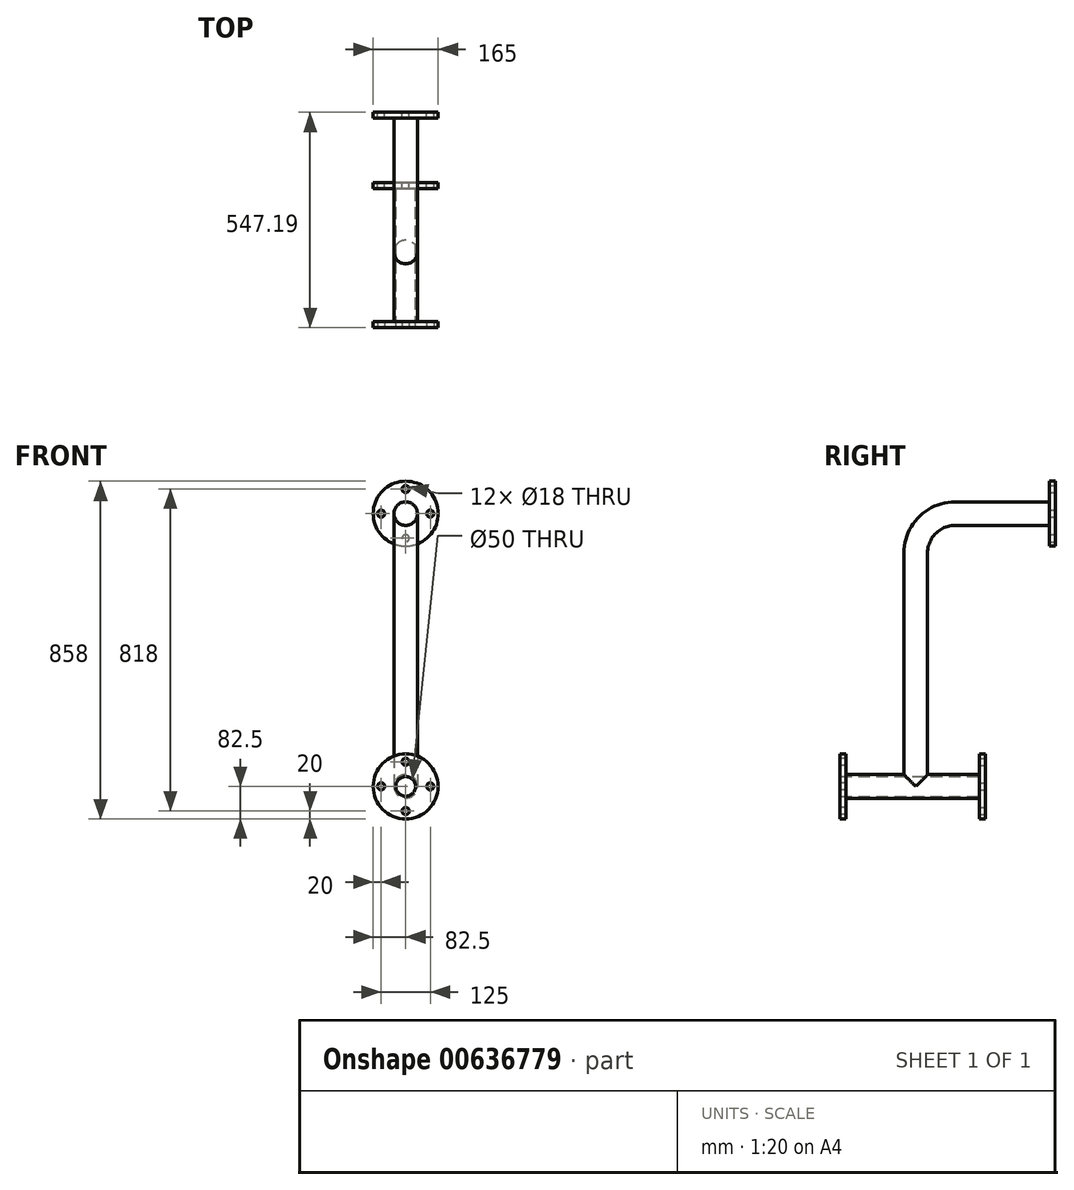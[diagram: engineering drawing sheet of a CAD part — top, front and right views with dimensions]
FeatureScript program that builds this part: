
annotation { "Feature Type Name" : "Feature", "Feature Type Description" : "" }
export const myFeature = defineFeature(function(context is Context, id is Id, definition is map)
    precondition{}
    {
        {
            var Q0;
            Q0=qCreatedBy(makeId("Front.planeOp"),FACE);
            var sketch = newSketch(context, id + "F0", { "sketchPlane" : qUnion([Q0])});
            skCircle(sketch, "E0", {"center": v(0, 0) * mm, "radius": 82.5 * mm});
            skCircle(sketch, "E1", {"center": v(0, 0) * mm, "radius": 30 * mm});
            skSolve(sketch);
        }
        {
            var Q0;
            Q0=qCreatedBy(makeId("Right.planeOp"),FACE);
            var sketch = newSketch(context, id + "F1", { "sketchPlane" : qUnion([Q0])});
            skLineSegment(sketch, "E2", {"start": v(0, 0) * mm, "end": v(-255, 0) * mm});
            skLineSegment(sketch, "E3", {"start": v(-355, -100) * mm, "end": v(-355, -693) * mm});
            skLineSegment(sketch, "E4", {"start": v(-355, -693) * mm, "end": v(-178.56, -693) * mm});
            skLineSegment(sketch, "E5", {"start": v(-355, -693) * mm, "end": v(-547.2, -693) * mm});
            skPoint(sketch, "E6.visualSharp", {"position": v(-355, 0) * mm});
            skArc(sketch, "E6.filletArc", {"start": v(-255, 0) * mm, "mid": v(-325.71, -29.29) * mm, "end": v(-355, -100) * mm});
            skSolve(sketch);
        }
        {
            var Q0;
            Q0=makeQuery(id+"F0.imprint","IMPRINT",FACE,{"disambiguationData":[TD([[makeQuery(id+"F0.imprint","IMPRINT",EDGE,{"derivedFrom":sQuery(id+"F0.wireOp",EDGE,"E1")}),1.0]])]});
            var Q1;
            Q1=sQuery(id+"F1.wireOp",EDGE,"E2");
            var Q2;
            Q2=sQuery(id+"F1.wireOp",EDGE,"E6.filletArc");
            var Q3;
            Q3=sQuery(id+"F1.wireOp",EDGE,"E3");
            var Q4;
            Q4=sQuery(id+"F1.wireOp",EDGE,"E5");
            sweep(context, id + "F2", {"profiles" : qUnion([Q0]), "path" : qUnion([Q1, Q2, Q3, Q4])});
        }
        {
            var Q0;
            Q0=makeQuery(id+"F2.opSweep","CAP_FACE",FACE,{"disambiguationData":[OSD([sQuery(id+"F0.wireOp",EDGE,"E1"),sQuery(id+"F1.wireOp",VERTEX,"E5.end")])],"isStart":false});
            var sketch = newSketch(context, id + "F3", { "sketchPlane" : qUnion([Q0])});
            skCircle(sketch, "E7", {"center": v(0, -693) * mm, "radius": 30 * mm});
            skSolve(sketch);
        }
        {
            var Q0;
            Q0=makeQuery(id+"F3.imprint","IMPRINT",FACE,{"disambiguationData":[TD([[makeQuery(id+"F3.imprint","IMPRINT",EDGE,{"derivedFrom":sQuery(id+"F3.wireOp",EDGE,"E7")}),1.0]])]});
            var Q1;
            Q1=sQuery(id+"F1.wireOp",EDGE,"E5");
            var Q2;
            Q2=sQuery(id+"F1.wireOp",EDGE,"E4");
            sweep(context, id + "F4", {"operationType" : NewBodyOperationType.ADD, "profiles" : qUnion([Q0]), "path" : qUnion([Q1, Q2])});
        }
        {
            var Q0;
            Q0=makeQuery(id+"F0.imprint","IMPRINT",FACE,{"disambiguationData":[TD([[makeQuery(id+"F0.imprint","IMPRINT",EDGE,{"derivedFrom":sQuery(id+"F0.wireOp",EDGE,"E0")}),1.0]])]});
            extrude(context, id + "F5", {"entities" : qUnion([Q0]), "operationType" : NewBodyOperationType.ADD, "depth" : 15 * mm, "offsetDistance" : 25 * mm});
        }
        {
            var Q0;
            Q0=makeQuery(id+"F0.imprint","IMPRINT",FACE,{"disambiguationData":[TD([[makeQuery(id+"F0.imprint","IMPRINT",EDGE,{"derivedFrom":sQuery(id+"F0.wireOp",EDGE,"E0")}),1.0]])]});
            var sketch = newSketch(context, id + "F6", { "sketchPlane" : qUnion([Q0])});
            skCircle(sketch, "E8", {"center": v(0, 62.5) * mm, "radius": 9 * mm});
            skCircle(sketch, "E9.1.0", {"center": v(-62.5, 0) * mm, "radius": 9 * mm});
            skCircle(sketch, "E9.2.0", {"center": v(0, -62.5) * mm, "radius": 9 * mm});
            skCircle(sketch, "E9.3.0", {"center": v(62.5, 0) * mm, "radius": 9 * mm});
            skPoint(sketch, "E9.center", {"position": v(0, 0) * mm});
            skSolve(sketch);
        }
        {
            var Q0;
            Q0 = qSketchRegion(id + "F6", true);
            extrude(context, id + "F7", {"entities" : qUnion([Q0]), "operationType" : NewBodyOperationType.REMOVE, "depth" : 25 * mm, "offsetDistance" : 25 * mm});
        }
        {
            var Q0;
            Q0=makeQuery(id+"F2.opSweep","CAP_FACE",FACE,{"disambiguationData":[OSD([sQuery(id+"F0.wireOp",EDGE,"E1"),sQuery(id+"F1.wireOp",VERTEX,"E5.end")])],"isStart":false});
            var sketch = newSketch(context, id + "F8", { "sketchPlane" : qUnion([Q0])});
            skCircle(sketch, "E10", {"center": v(0, -693) * mm, "radius": 82.5 * mm});
            skCircle(sketch, "E11", {"center": v(0, -630.5) * mm, "radius": 9 * mm});
            skCircle(sketch, "E12.1.0", {"center": v(-62.5, -693) * mm, "radius": 9 * mm});
            skCircle(sketch, "E12.2.0", {"center": v(0, -755.5) * mm, "radius": 9 * mm});
            skCircle(sketch, "E12.3.0", {"center": v(62.5, -693) * mm, "radius": 9 * mm});
            skSolve(sketch);
        }
        {
            var Q0;
            Q0=makeQuery(id+"F8.imprint","IMPRINT",FACE,{"disambiguationData":[TD([[makeQuery(id+"F8.imprint","IMPRINT",EDGE,{"derivedFrom":sQuery(id+"F8.wireOp",EDGE,"E10")}),1.0]])]});
            extrude(context, id + "F9", {"entities" : qUnion([Q0]), "operationType" : NewBodyOperationType.ADD, "oppositeDirection" : true, "depth" : 15 * mm, "offsetDistance" : 25 * mm});
        }
        {
            var Q0;
            Q0=makeQuery(id+"F4.opSweep","CAP_FACE",FACE,{"disambiguationData":[OSD([sQuery(id+"F1.wireOp",VERTEX,"E4.end"),sQuery(id+"F3.wireOp",EDGE,"E7")])],"isStart":false});
            var sketch = newSketch(context, id + "F10", { "sketchPlane" : qUnion([Q0])});
            skCircle(sketch, "E13.0", {"center": v(0, -693) * mm, "radius": 82.5 * mm});
            skCircle(sketch, "E14.0", {"center": v(0, -755.5) * mm, "radius": 9 * mm});
            skCircle(sketch, "E15.0", {"center": v(-62.5, -693) * mm, "radius": 9 * mm});
            skCircle(sketch, "E16.0", {"center": v(0, -630.5) * mm, "radius": 9 * mm});
            skCircle(sketch, "E17.0", {"center": v(62.5, -693) * mm, "radius": 9 * mm});
            skSolve(sketch);
        }
        {
            var Q0;
            Q0=makeQuery(id+"F10.imprint","IMPRINT",FACE,{"disambiguationData":[TD([[makeQuery(id+"F10.imprint","IMPRINT",EDGE,{"derivedFrom":sQuery(id+"F10.wireOp",EDGE,"E14.0")}),-1.0]])]});
            extrude(context, id + "F11", {"entities" : qUnion([Q0]), "operationType" : NewBodyOperationType.ADD, "oppositeDirection" : true, "depth" : 15 * mm, "offsetDistance" : 25 * mm});
        }
        {
            var Q0;
            {var subQ0=sQuery(id+"F3.wireOp",EDGE,"E7");var subQ1=sQuery(id+"F1.wireOp",VERTEX,"E4.end");Q0=makeQuery(id+"F11.boolean.opBoolean","MERGE",FACE,{"derivedFrom":[makeQuery(id+"F4.opSweep","CAP_FACE",FACE,{"disambiguationData":[OSD([subQ1,subQ0])],"isStart":false}),makeQuery(id+"F11.opExtrude","CAP_FACE",FACE,{"disambiguationData":[OSD([subQ1,subQ0,sQuery(id+"F10.wireOp",EDGE,"E14.0"),sQuery(id+"F10.wireOp",EDGE,"E13.0"),sQuery(id+"F10.wireOp",EDGE,"E15.0"),sQuery(id+"F10.wireOp",EDGE,"E16.0"),sQuery(id+"F10.wireOp",EDGE,"E17.0")])],"isStart":true})]});}
            var sketch = newSketch(context, id + "F12", { "sketchPlane" : qUnion([Q0])});
            skCircle(sketch, "E18", {"center": v(0, -693) * mm, "radius": 25 * mm});
            skSolve(sketch);
        }
        {
            var Q0;
            Q0=makeQuery(id+"F12.imprint","IMPRINT",FACE,{"disambiguationData":[TD([[makeQuery(id+"F12.imprint","IMPRINT",EDGE,{"derivedFrom":sQuery(id+"F12.wireOp",EDGE,"E18")}),1.0]])]});
            extrude(context, id + "F13", {"entities" : qUnion([Q0]), "operationType" : NewBodyOperationType.REMOVE, "endBound" : BoundingType.UP_TO_NEXT, "oppositeDirection" : true, "depth" : 25 * mm, "offsetDistance" : 25 * mm});
        }
    });
